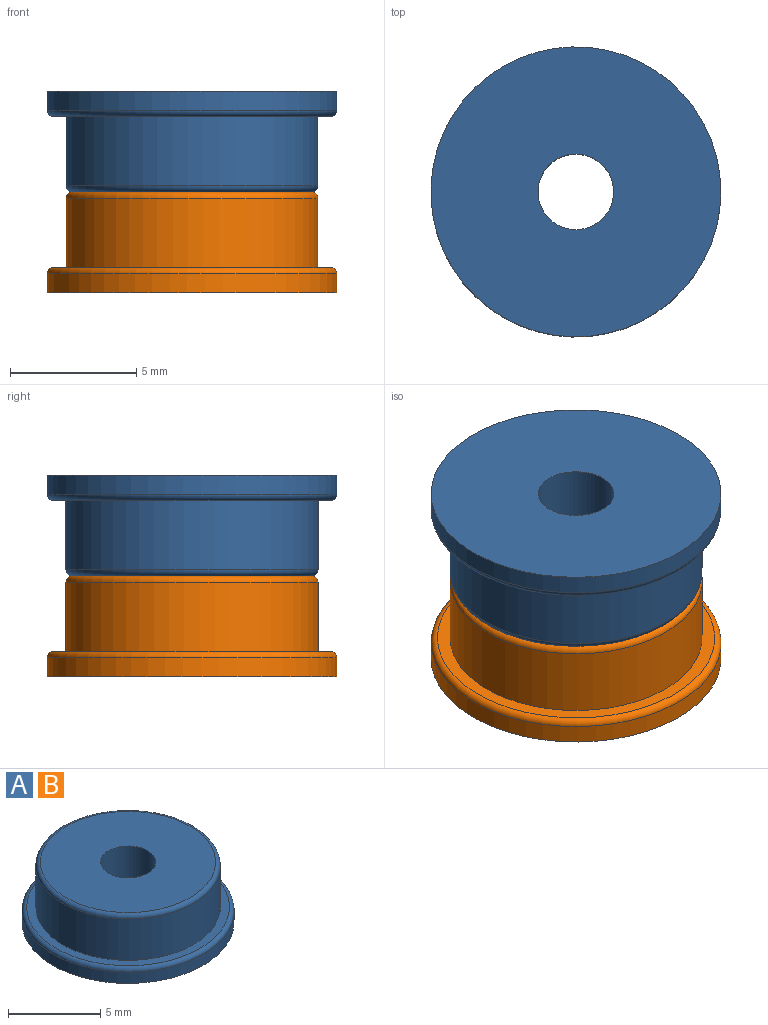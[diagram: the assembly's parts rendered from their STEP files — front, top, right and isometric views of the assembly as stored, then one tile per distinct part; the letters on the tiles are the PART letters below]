
ASSEMBLY  parts=2 mates=1
PART A: 8 faces, bbox 12.4x12.4x4 mm
  f0: cylinder r=5.75mm len=11.5mm, axis (0,0,-1), area 27.1mm2, adj f2,f7
  f1: plane 11x11mm, normal (0,0,1), area 16.5mm2, adj f3,f7
  f2: plane 11.5x11.5mm, normal (0,0,-1), area 96.8mm2, adj f0,f5
  f3: cylinder r=5mm len=10mm, axis (0,0,-1), area 86.4mm2, adj f1,f6
  f4: plane 9.5x9.5mm, normal (0,0,1), area 63.8mm2, adj f5,f6
  f5: cylinder r=1.5mm len=4mm, axis (0,0,1), area 37.7mm2, adj f2,f4
  f6: torus R=4.75mm, axis (0,0,1), area 12.1mm2, adj f3,f4
  f7: torus R=5.5mm, axis (0,0,1), area 14mm2, adj f0,f1
PART B: same geometry as A
PLACE A rot(axis=(1,0,0),180deg) t=(-1.64,-0.04,7.36)mm
PLACE B t=(-1.64,-0.04,-0.64)mm
MATE fastened A.f5 <-> B.f5  axis (0,0,-1) through (-1.64,-0.04,3.36)mm
